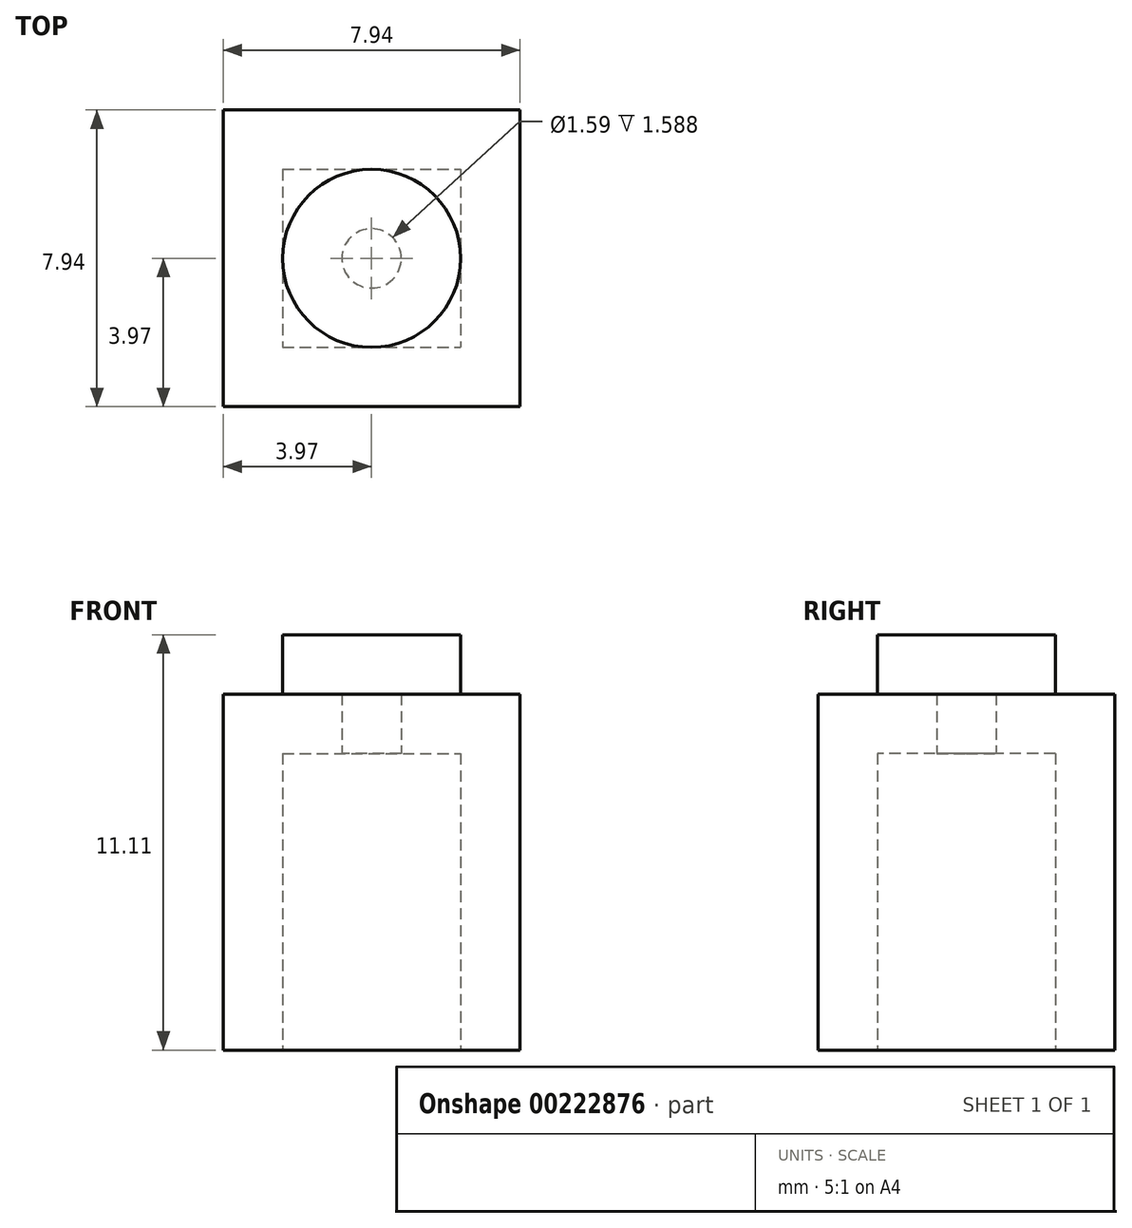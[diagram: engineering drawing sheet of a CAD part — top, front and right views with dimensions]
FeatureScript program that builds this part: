
annotation { "Feature Type Name" : "Feature", "Feature Type Description" : "" }
export const myFeature = defineFeature(function(context is Context, id is Id, definition is map)
    precondition{}
    {
        {
            var Q0;
            Q0=qCreatedBy(makeId("Top.planeOp"),FACE);
            var sketch = newSketch(context, id + "F0", { "sketchPlane" : qUnion([Q0])});
            skLineSegment(sketch, "E0.bottom", {"start": v(-3.97, 3.97) * mm, "end": v(3.97, 3.97) * mm});
            skLineSegment(sketch, "E0.top", {"start": v(-3.97, -3.97) * mm, "end": v(3.97, -3.97) * mm});
            skLineSegment(sketch, "E0.left", {"start": v(-3.97, 3.97) * mm, "end": v(-3.97, -3.97) * mm});
            skLineSegment(sketch, "E0.right", {"start": v(3.97, 3.97) * mm, "end": v(3.97, -3.97) * mm});
            skPoint(sketch, "E0.middle", {"position": v(0, 0) * mm});
            skCircle(sketch, "E1", {"center": v(0, 0) * mm, "radius": 2.38 * mm});
            skSolve(sketch);
        }
        {
            var Q0;
            Q0 = qSketchRegion(id + "F0", true);
            extrude(context, id + "F1", {"entities" : qUnion([Q0]), "depth" : 9.52 * mm});
        }
        {
            var Q0;
            Q0=makeQuery(id+"F0.imprint","IMPRINT",FACE,{"disambiguationData":[TD([[makeQuery(id+"F0.imprint","IMPRINT",EDGE,{"derivedFrom":sQuery(id+"F0.wireOp",EDGE,"E1")}),1.0]])]});
            extrude(context, id + "F2", {"entities" : qUnion([Q0]), "operationType" : NewBodyOperationType.ADD, "depth" : 11.1 * mm});
        }
        {
            var Q0;
            {var subQ0=sQuery(id+"F0.wireOp",EDGE,"E1");Q0=makeQuery(id+"F2.boolean.opBoolean","MERGE",FACE,{"derivedFrom":[makeQuery(id+"F1.opExtrude","CAP_FACE",FACE,{"disambiguationData":[OSD([sQuery(id+"F0.wireOp",EDGE,"E0.bottom"),sQuery(id+"F0.wireOp",EDGE,"E0.top"),sQuery(id+"F0.wireOp",EDGE,"E0.left"),sQuery(id+"F0.wireOp",EDGE,"E0.right"),subQ0])],"isStart":true}),makeQuery(id+"F2.opExtrude","CAP_FACE",FACE,{"disambiguationData":[OSD([subQ0])],"isStart":true})]});}
            shell(context, id + "F3", {"entities" : qUnion([Q0]), "thickness" : 1.59 * mm});
        }
    });
